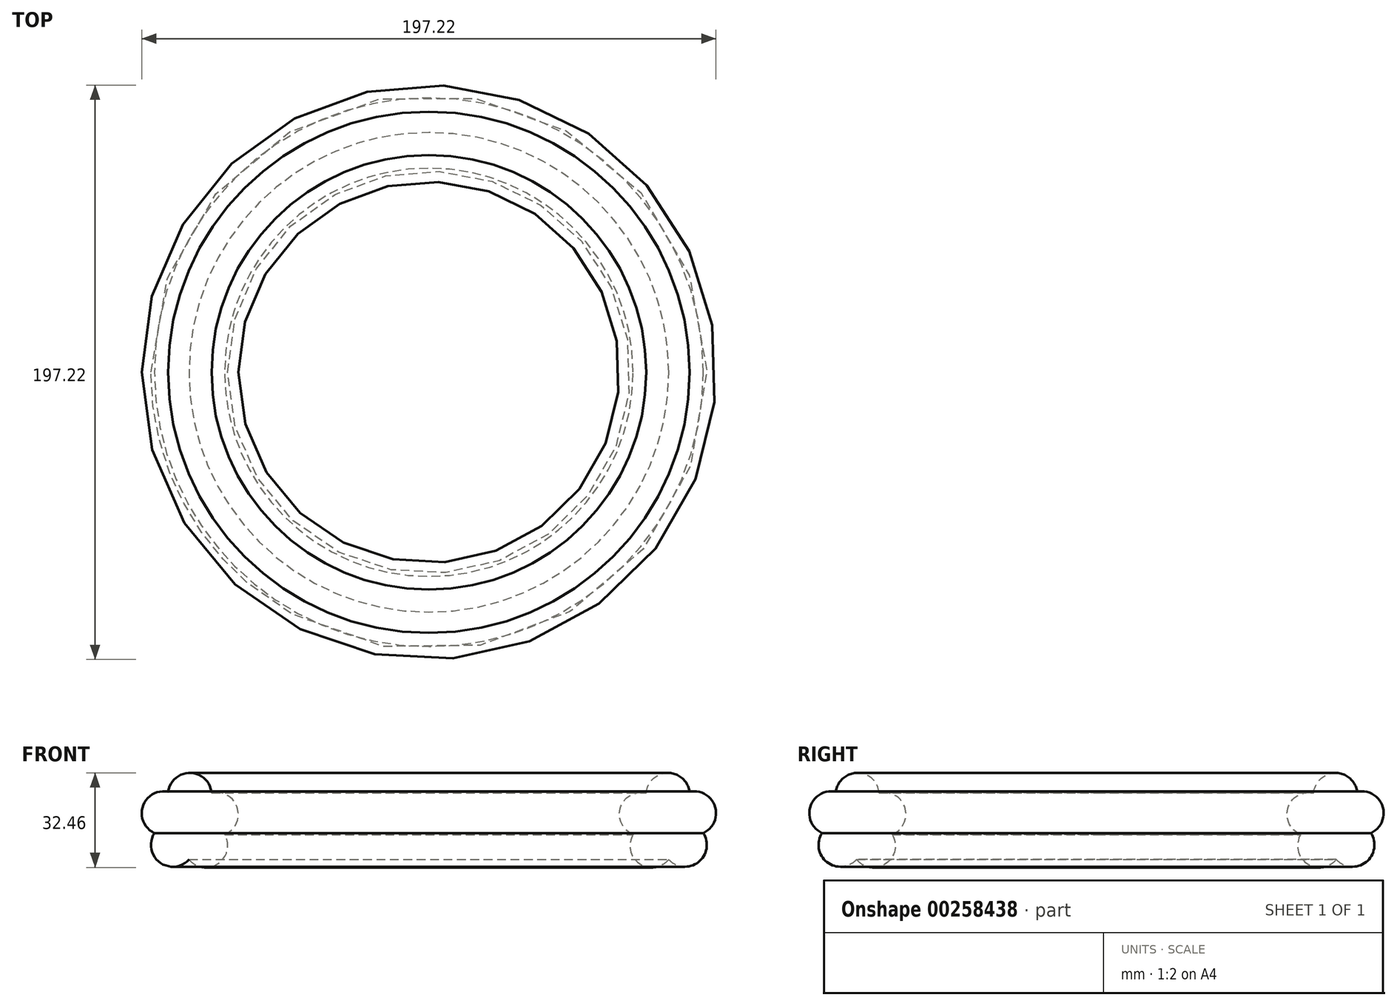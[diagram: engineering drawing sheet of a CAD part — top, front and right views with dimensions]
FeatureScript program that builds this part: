
annotation { "Feature Type Name" : "Feature", "Feature Type Description" : "" }
export const myFeature = defineFeature(function(context is Context, id is Id, definition is map)
    precondition{}
    {
        {
            var Q0;
            Q0=qCreatedBy(makeId("Front.planeOp"),FACE);
            var sketch = newSketch(context, id + "F0", { "sketchPlane" : qUnion([Q0])});
            skArc(sketch, "E0.1.0", {"start": v(-70.11, -6.91) * mm, "mid": v(-65.78, 2.3) * mm, "end": v(-74.6, 7.35) * mm});
            skArc(sketch, "E0.2.0", {"start": v(-82.36, -15.49) * mm, "mid": v(-72.28, -16.86) * mm, "end": v(-70.11, -6.91) * mm});
            skArc(sketch, "E0.3.0", {"start": v(-94.22, -6.39) * mm, "mid": v(-92.5, -16.41) * mm, "end": v(-82.36, -15.49) * mm});
            skPoint(sketch, "E0.center", {"position": v(-82.08, -2.85) * mm});
            skArc(sketch, "E1.trimOffspring", {"start": v(-89.52, 7.77) * mm, "mid": v(-98.22, 2.8) * mm, "end": v(-94.22, -6.39) * mm});
            skPoint(sketch, "E2.center.orphan", {"position": v(-82.08, -0.75) * mm});
            skArc(sketch, "E3.trimOffspring", {"start": v(-74.6, 7.35) * mm, "mid": v(-81.87, 14.25) * mm, "end": v(-89.52, 7.77) * mm});
            skLineSegment(sketch, "E4.trimOffspring", {"start": v(-87.85, -0.75) * mm, "end": v(-89.58, -0.75) * mm, "construction": true});
            skLineSegment(sketch, "E5", {"start": v(0, -51.12) * mm, "end": v(0, 66.75) * mm, "construction": true});
            skLineSegment(sketch, "E6", {"start": v(-82.08, -2.85) * mm, "end": v(0, -2.85) * mm, "construction": true});
            skSolve(sketch);
        }
        {
            var Q0;
            Q0=makeQuery(id+"F0.imprint","IMPRINT",FACE,{"disambiguationData":[TD([[makeQuery(id+"F0.imprint","IMPRINT",EDGE,{"derivedFrom":sQuery(id+"F0.wireOp",EDGE,"E0.1.0")}),1.0]])]});
            var Q1;
            Q1=sQuery(id+"F0.wireOp",EDGE,"E5");
            revolve(context, id + "F1", {"entities" : qUnion([Q0]), "axis" : qUnion([Q1]), "revolveType" : RevolveType.FULL});
        }
    });
